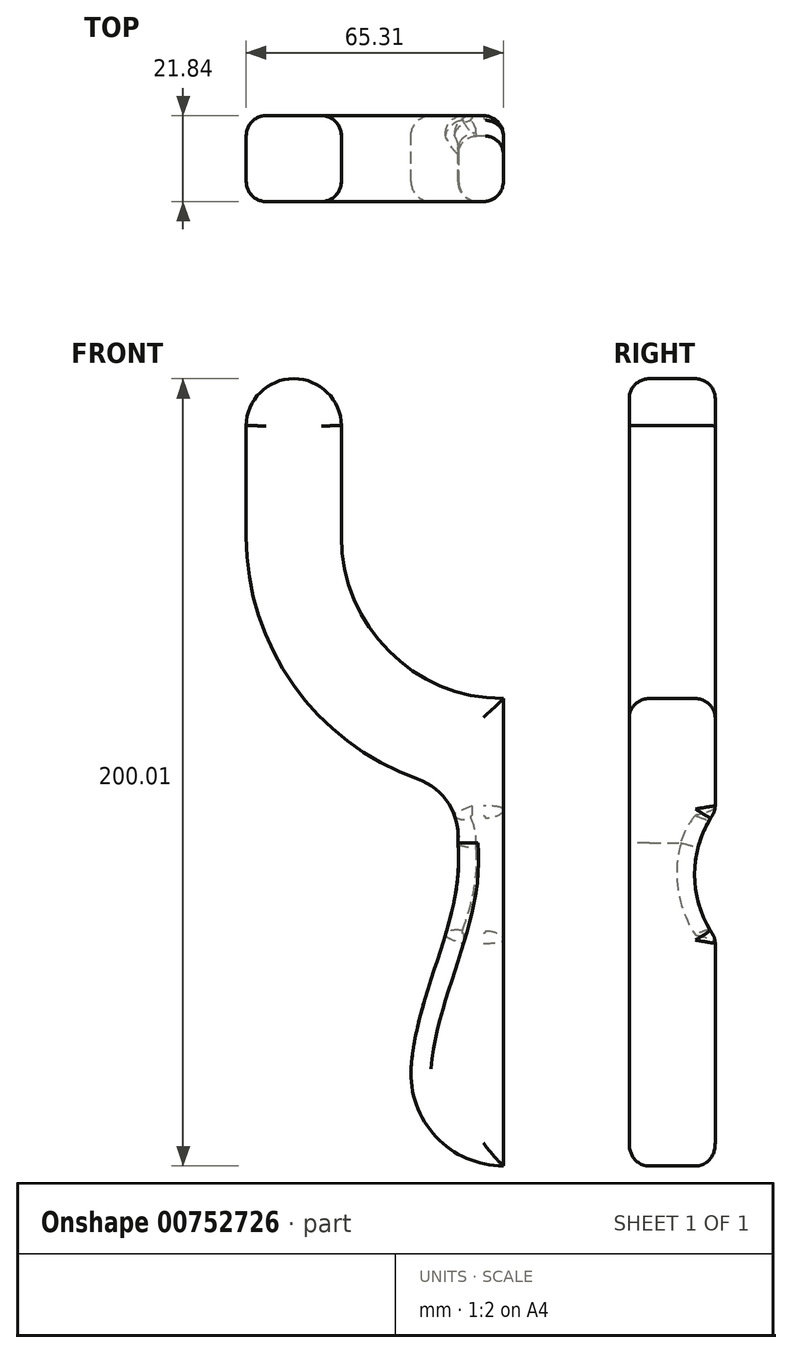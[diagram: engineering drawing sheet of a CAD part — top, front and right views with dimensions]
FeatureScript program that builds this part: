
annotation { "Feature Type Name" : "Feature", "Feature Type Description" : "" }
export const myFeature = defineFeature(function(context is Context, id is Id, definition is map)
    precondition{}
    {
        {
            var Q0;
            Q0=qCreatedBy(makeId("Front.planeOp"),FACE);
            var sketch = newSketch(context, id + "F0", { "sketchPlane" : qUnion([Q0])});
            skLineSegment(sketch, "E0", {"start": v(0, -71.64) * mm, "end": v(0, 23.65) * mm, "construction": true});
            skArc(sketch, "E1", {"start": v(-41.15, 64.8) * mm, "mid": v(-29.1, 35.7) * mm, "end": v(0, 23.65) * mm});
            skArc(sketch, "E2", {"start": v(-23.39, -70.11) * mm, "mid": v(-17.1, -87.66) * mm, "end": v(0, -95.08) * mm});
            skArc(sketch, "E3", {"start": v(-11.53, -12.99) * mm, "mid": v(-13.84, -3.1) * mm, "end": v(-21.77, 3.23) * mm});
            skFitSpline(sketch, "E4", {"points": [v(-23.39, -70.11) * mm, v(-11.53, -12.99) * mm], "startDerivative": vector(3.85, 58.87) * mm, "endDerivative": vector(-5.86, 56.73) * mm});
            skLineSegment(sketch, "E5.right", {"start": v(-65.3, 64.8) * mm, "end": v(-65.3, 92.98) * mm});
            skLineSegment(sketch, "E6", {"start": v(-41.15, 64.8) * mm, "end": v(-41.15, 92.98) * mm});
            skArc(sketch, "E7", {"start": v(-41.15, 92.98) * mm, "mid": v(-53.23, 104.93) * mm, "end": v(-65.3, 92.98) * mm});
            skArc(sketch, "E8.trimOffspring", {"start": v(-65.3, 64.8) * mm, "mid": v(-53.32, 27.1) * mm, "end": v(-21.77, 3.23) * mm});
            skPoint(sketch, "E9.trimOffspring.end.orphan", {"position": v(-41.15, 160.62) * mm});
            skLineSegment(sketch, "E10.trimOffspring", {"start": v(0, 23.65) * mm, "end": v(0, -122.67) * mm});
            skPoint(sketch, "E11.start.orphan", {"position": v(0, 155.85) * mm});
            skPoint(sketch, "E12.orphan", {"position": v(41.15, 160.62) * mm});
            skPoint(sketch, "E5.left.start.orphan", {"position": v(65.3, 64.8) * mm});
            skArc(sketch, "E13.MirrorCS", {"start": v(23.39, -70.11) * mm, "mid": v(17.1, -87.66) * mm, "end": v(0, -95.08) * mm});
            skFitSpline(sketch, "E14.MirrorCS", {"points": [v(23.39, -70.11) * mm, v(11.53, -12.99) * mm], "startDerivative": vector(-3.85, 58.87) * mm, "endDerivative": vector(5.86, 56.73) * mm});
            skArc(sketch, "E15.MirrorCS", {"start": v(11.53, -12.99) * mm, "mid": v(13.84, -3.1) * mm, "end": v(21.77, 3.23) * mm});
            skArc(sketch, "E16.MirrorCS", {"start": v(65.3, 64.8) * mm, "mid": v(53.32, 27.1) * mm, "end": v(21.77, 3.23) * mm});
            skLineSegment(sketch, "E17.MirrorCS", {"start": v(41.15, 64.8) * mm, "end": v(41.15, 92.98) * mm});
            skLineSegment(sketch, "E18.MirrorCS", {"start": v(65.3, 64.8) * mm, "end": v(65.3, 92.98) * mm});
            skArc(sketch, "E19.MirrorCS", {"start": v(41.15, 92.98) * mm, "mid": v(53.23, 104.93) * mm, "end": v(65.3, 92.98) * mm});
            skArc(sketch, "E20.MirrorCS", {"start": v(41.15, 64.8) * mm, "mid": v(29.1, 35.7) * mm, "end": v(0, 23.65) * mm});
            skSolve(sketch);
        }
        {
            var Q0;
            {var subQ0=sQuery(id+"F0.wireOp",EDGE,"E13.MirrorCS");Q0=makeQuery(id+"F0.imprint","IMPRINT",FACE,{"disambiguationData":[TD([[makeQuery(id+"F0.imprint","IMPRINT",EDGE,{"derivedFrom":subQ0}),-1.0]])]});}
            var Q1;
            {var subQ1=sQuery(id+"F0.wireOp",EDGE,"E1");Q1=makeQuery(id+"F0.imprint","IMPRINT",FACE,{"disambiguationData":[TD([[makeQuery(id+"F0.imprint","IMPRINT",EDGE,{"derivedFrom":subQ1}),-1.0]])]});}
            extrude(context, id + "F1", {"entities" : qUnion([Q0, Q1]), "depth" : 21.84 * mm, "offsetDistance" : 25.4 * mm});
        }
        {
            var Q0;
            Q0=makeQuery(id+"F1.opExtrude","CAP_FACE",FACE,{"disambiguationData":[OSD([sQuery(id+"F0.wireOp",EDGE,"E1"),sQuery(id+"F0.wireOp",EDGE,"E2"),sQuery(id+"F0.wireOp",EDGE,"E3"),sQuery(id+"F0.wireOp",EDGE,"E4"),sQuery(id+"F0.wireOp",EDGE,"E5.right"),sQuery(id+"F0.wireOp",EDGE,"E6"),sQuery(id+"F0.wireOp",EDGE,"E7"),sQuery(id+"F0.wireOp",EDGE,"E8.trimOffspring"),sQuery(id+"F0.wireOp",EDGE,"E13.MirrorCS"),sQuery(id+"F0.wireOp",EDGE,"E14.MirrorCS"),sQuery(id+"F0.wireOp",EDGE,"E15.MirrorCS"),sQuery(id+"F0.wireOp",EDGE,"E16.MirrorCS"),sQuery(id+"F0.wireOp",EDGE,"E17.MirrorCS"),sQuery(id+"F0.wireOp",EDGE,"E18.MirrorCS"),sQuery(id+"F0.wireOp",EDGE,"E19.MirrorCS"),sQuery(id+"F0.wireOp",EDGE,"E20.MirrorCS")])],"isStart":false});
            var Q1;
            Q1=makeQuery(id+"F1.opExtrude","CAP_FACE",FACE,{"disambiguationData":[OSD([sQuery(id+"F0.wireOp",EDGE,"E1"),sQuery(id+"F0.wireOp",EDGE,"E2"),sQuery(id+"F0.wireOp",EDGE,"E3"),sQuery(id+"F0.wireOp",EDGE,"E4"),sQuery(id+"F0.wireOp",EDGE,"E5.right"),sQuery(id+"F0.wireOp",EDGE,"E6"),sQuery(id+"F0.wireOp",EDGE,"E7"),sQuery(id+"F0.wireOp",EDGE,"E8.trimOffspring"),sQuery(id+"F0.wireOp",EDGE,"E13.MirrorCS"),sQuery(id+"F0.wireOp",EDGE,"E14.MirrorCS"),sQuery(id+"F0.wireOp",EDGE,"E15.MirrorCS"),sQuery(id+"F0.wireOp",EDGE,"E16.MirrorCS"),sQuery(id+"F0.wireOp",EDGE,"E17.MirrorCS"),sQuery(id+"F0.wireOp",EDGE,"E18.MirrorCS"),sQuery(id+"F0.wireOp",EDGE,"E19.MirrorCS"),sQuery(id+"F0.wireOp",EDGE,"E20.MirrorCS")])],"isStart":true});
            fillet(context, id + "F2", {"entities" : qUnion([Q0, Q1]), "radius" : 5.08 * mm, "tangentPropagation" : true, "allowEdgeOverflow" : false});
        }
        {
            var Q0;
            Q0=qCreatedBy(makeId("Right.planeOp"),FACE);
            var sketch = newSketch(context, id + "F3", { "sketchPlane" : qUnion([Q0])});
            skCircle(sketch, "E21", {"center": v(22.14, -21.06) * mm, "radius": 27.36 * mm});
            skSolve(sketch);
        }
        {
            var Q0;
            Q0=makeQuery(id+"F3.imprint","IMPRINT",FACE,{"disambiguationData":[TD([[makeQuery(id+"F3.imprint","IMPRINT",EDGE,{"derivedFrom":sQuery(id+"F3.wireOp",EDGE,"E21")}),1.0]])]});
            extrude(context, id + "F4", {"entities" : qUnion([Q0]), "operationType" : NewBodyOperationType.REMOVE, "depth" : 45.2 * mm, "offsetDistance" : 25.4 * mm, "symmetric" : true});
        }
        {
            var Q0;
            Q0=makeQuery(id+"F4.boolean.opBoolean","COPY",FACE,{"derivedFrom":makeQuery(id+"F4.opExtrude","SWEPT_FACE",FACE,{"disambiguationData":[OSD([sQuery(id+"F3.wireOp",EDGE,"E21")])]})});
            fillet(context, id + "F5", {"entities" : qUnion([Q0]), "radius" : 4.55 * mm, "tangentPropagation" : true, "allowEdgeOverflow" : false});
        }
    });
